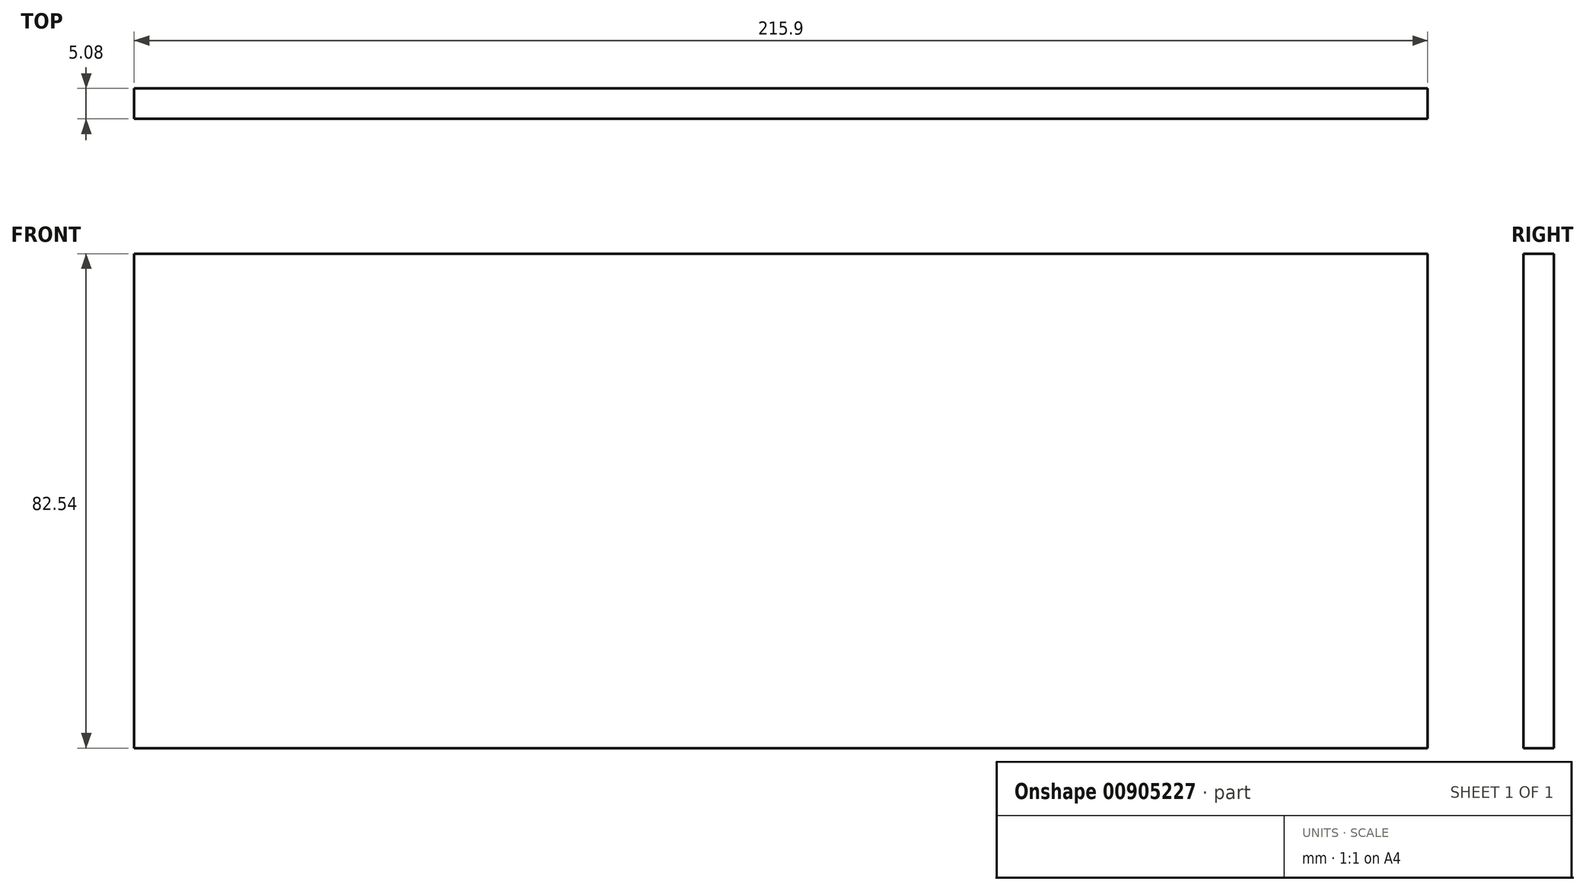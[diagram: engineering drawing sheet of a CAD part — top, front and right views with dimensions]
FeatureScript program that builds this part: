
annotation { "Feature Type Name" : "Feature", "Feature Type Description" : "" }
export const myFeature = defineFeature(function(context is Context, id is Id, definition is map)
    precondition{}
    {
        {
            var Q0;
            Q0=qCreatedBy(makeId("Front.planeOp"),FACE);
            var sketch = newSketch(context, id + "F0", { "sketchPlane" : qUnion([Q0])});
            skLineSegment(sketch, "E0.bottom", {"start": v(-107.95, 41.27) * mm, "end": v(107.95, 41.28) * mm});
            skLineSegment(sketch, "E0.top", {"start": v(-107.95, -41.28) * mm, "end": v(107.95, -41.27) * mm});
            skLineSegment(sketch, "E0.left", {"start": v(-107.95, 41.27) * mm, "end": v(-107.95, -41.28) * mm});
            skLineSegment(sketch, "E0.right", {"start": v(107.95, 41.28) * mm, "end": v(107.95, -41.27) * mm});
            skSolve(sketch);
        }
        {
            var Q0;
            Q0=makeQuery(id+"F0.imprint","IMPRINT",FACE,{"disambiguationData":[TD([[makeQuery(id+"F0.imprint","IMPRINT",EDGE,{"derivedFrom":sQuery(id+"F0.wireOp",EDGE,"E0.bottom")}),-1.0]])]});
            var sketch = newSketch(context, id + "F1", { "sketchPlane" : qUnion([Q0])});
            skLineSegment(sketch, "E1.bottom", {"start": v(-40.64, 37.78) * mm, "end": v(-15.24, 37.78) * mm});
            skLineSegment(sketch, "E1.top", {"start": v(-40.64, 1.27) * mm, "end": v(-15.24, 1.27) * mm});
            skLineSegment(sketch, "E1.left", {"start": v(-40.64, 37.78) * mm, "end": v(-40.64, 1.27) * mm});
            skLineSegment(sketch, "E1.right", {"start": v(-15.24, 37.78) * mm, "end": v(-15.24, 1.27) * mm});
            skArc(sketch, "E2", {"start": v(-34.3, 28.65) * mm, "mid": v(-27.94, 8.41) * mm, "end": v(-21.59, 28.65) * mm});
            skPoint(sketch, "E2.centerSnap0", {"position": v(-15.24, 19.53) * mm});
            skPoint(sketch, "E2.centerSnap1", {"position": v(-27.94, 37.78) * mm});
            skCircle(sketch, "E3", {"center": v(-36.07, 33.21) * mm, "radius": 1.59 * mm});
            skCircle(sketch, "E4", {"center": v(-19.81, 5.84) * mm, "radius": 1.59 * mm});
            skArc(sketch, "E5", {"start": v(-21.59, 30.24) * mm, "mid": v(-27.94, 31.98) * mm, "end": v(-34.3, 30.24) * mm});
            skLineSegment(sketch, "E6", {"start": v(-34.29, 30.24) * mm, "end": v(-34.29, 28.65) * mm});
            skLineSegment(sketch, "E7", {"start": v(-21.59, 30.24) * mm, "end": v(-21.59, 28.65) * mm});
            skSolve(sketch);
        }
        {
            var Q0;
            Q0=makeQuery(id+"F0.imprint","IMPRINT",FACE,{"disambiguationData":[TD([[makeQuery(id+"F0.imprint","IMPRINT",EDGE,{"derivedFrom":sQuery(id+"F0.wireOp",EDGE,"E0.bottom")}),-1.0]])]});
            extrude(context, id + "F2", {"entities" : qUnion([Q0]), "depth" : 5.08 * mm, "offsetDistance" : 25.4 * mm});
        }
    });
